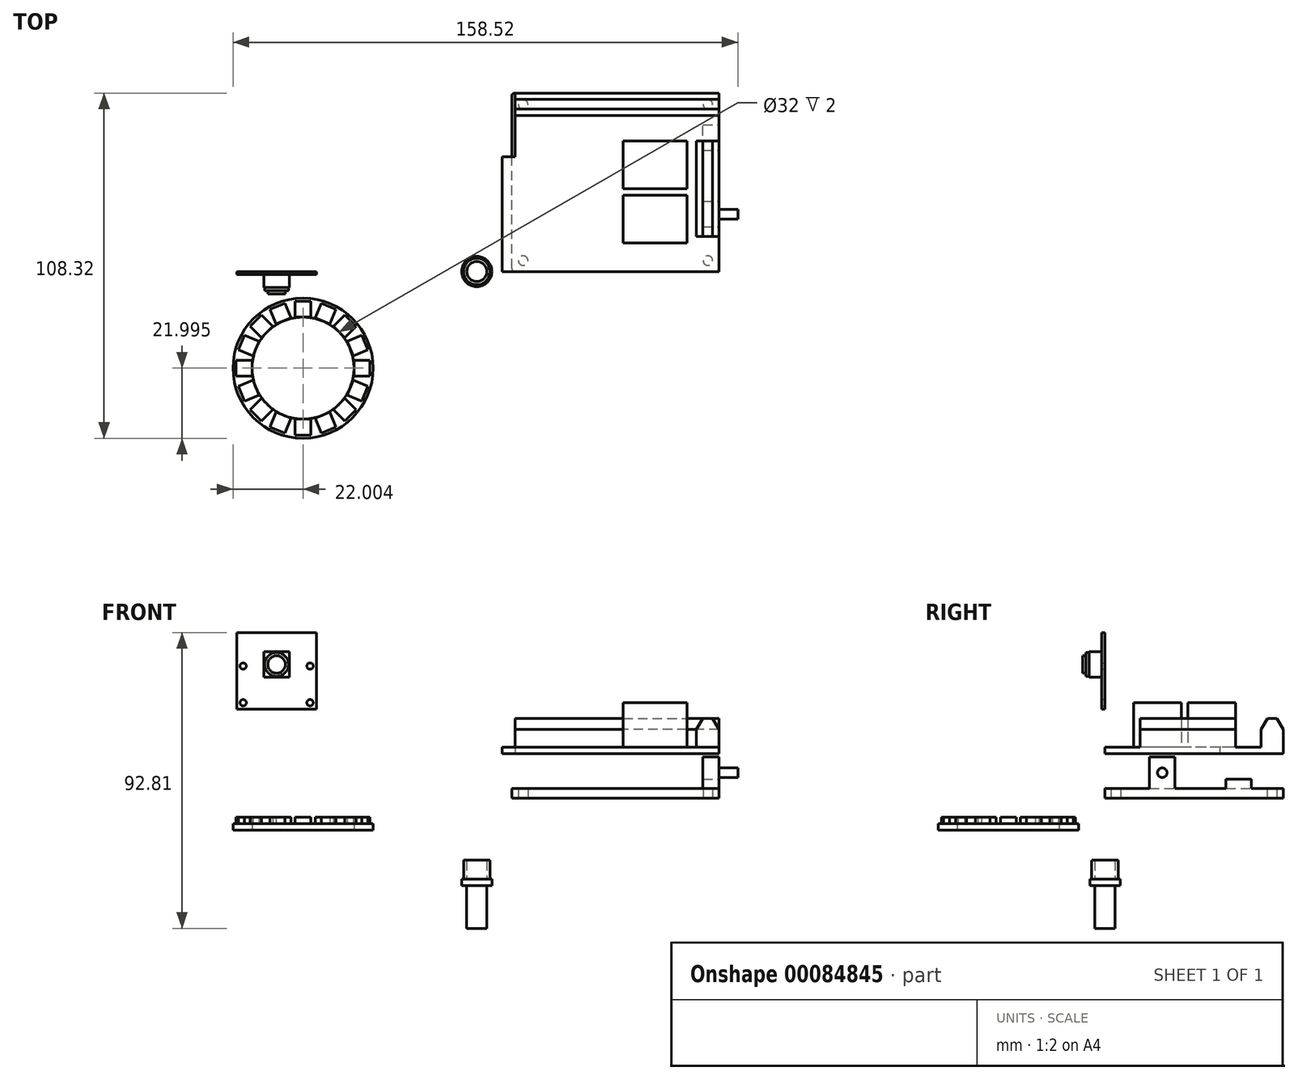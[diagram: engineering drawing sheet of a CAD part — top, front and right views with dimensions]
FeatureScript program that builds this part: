
annotation { "Feature Type Name" : "Feature", "Feature Type Description" : "" }
export const myFeature = defineFeature(function(context is Context, id is Id, definition is map)
    precondition{}
    {
        {
            var Q0;
            Q0=qCreatedBy(makeId("Top.planeOp"),FACE);
            cPlane(context, id + "F0", {"entities" : qUnion([Q0]), "cplaneType" : CPlaneType.OFFSET, "offset" : 10 * mm, "width" : 150 * mm, "height" : 150 * mm});
        }
        {
            var Q0;
            Q0=qCreatedBy(id+"F0.planeOp",FACE);
            var sketch = newSketch(context, id + "F1", { "sketchPlane" : qUnion([Q0])});
            skLineSegment(sketch, "E0.bottom", {"start": v(21, 0) * mm, "end": v(84, 0) * mm});
            skLineSegment(sketch, "E0.top", {"start": v(21, 56) * mm, "end": v(84, 56) * mm});
            skLineSegment(sketch, "E0.left", {"start": v(20, 1) * mm, "end": v(20, 55) * mm});
            skLineSegment(sketch, "E0.right", {"start": v(85, 1) * mm, "end": v(85, 55) * mm});
            skCircle(sketch, "E1", {"center": v(23.58, 52.42) * mm, "radius": 1.5 * mm});
            skCircle(sketch, "E2.0.1.0", {"center": v(23.58, 3.42) * mm, "radius": 1.5 * mm});
            skCircle(sketch, "E2.1.0.0", {"center": v(81.58, 52.42) * mm, "radius": 1.5 * mm});
            skCircle(sketch, "E2.1.1.0", {"center": v(81.58, 3.42) * mm, "radius": 1.5 * mm});
            skLineSegment(sketch, "E2.direction1", {"start": v(23.58, 52.42) * mm, "end": v(81.58, 52.42) * mm, "construction": true});
            skLineSegment(sketch, "E2.direction2", {"start": v(23.58, 52.42) * mm, "end": v(23.58, 3.42) * mm, "construction": true});
            skPoint(sketch, "E3.visualSharp", {"position": v(85, 56) * mm});
            skArc(sketch, "E3.filletArc", {"start": v(85, 55) * mm, "mid": v(84.7, 55.7) * mm, "end": v(84, 56) * mm});
            skPoint(sketch, "E4.visualSharp", {"position": v(85, 0) * mm});
            skArc(sketch, "E4.filletArc", {"start": v(84, 0) * mm, "mid": v(84.7, 0.3) * mm, "end": v(85, 1) * mm});
            skPoint(sketch, "E5.visualSharp", {"position": v(20, 0) * mm});
            skArc(sketch, "E5.filletArc", {"start": v(20, 1) * mm, "mid": v(20.3, 0.3) * mm, "end": v(21, 0) * mm});
            skPoint(sketch, "E6.visualSharp", {"position": v(20, 56) * mm});
            skArc(sketch, "E6.filletArc", {"start": v(21, 56) * mm, "mid": v(20.3, 55.7) * mm, "end": v(20, 55) * mm});
            skSolve(sketch);
        }
        {
            var Q0;
            Q0=qSketchRegion(id+"F1",true);
            extrude(context, id + "F2", {"entities" : qUnion([Q0]), "depth" : 3 * mm});
        }
        {
            var Q0;
            Q0=makeQuery(id+"F2.opExtrude","SWEPT_FACE",FACE,{"disambiguationData":[OSD([sQuery(id+"F1.wireOp",EDGE,"E0.right")])]});
            var sketch = newSketch(context, id + "F3", { "sketchPlane" : qUnion([Q0])});
            skLineSegment(sketch, "E7.bottom", {"start": v(14, 13) * mm, "end": v(22, 13) * mm});
            skLineSegment(sketch, "E7.top", {"start": v(14, 23) * mm, "end": v(22, 23) * mm});
            skLineSegment(sketch, "E7.left", {"start": v(14, 13) * mm, "end": v(14, 23) * mm});
            skLineSegment(sketch, "E7.right", {"start": v(22, 13) * mm, "end": v(22, 23) * mm});
            skLineSegment(sketch, "E8.bottom", {"start": v(38, 13) * mm, "end": v(46, 13) * mm});
            skLineSegment(sketch, "E8.top", {"start": v(38, 16) * mm, "end": v(46, 16) * mm});
            skLineSegment(sketch, "E8.left", {"start": v(38, 13) * mm, "end": v(38, 16) * mm});
            skLineSegment(sketch, "E8.right", {"start": v(46, 13) * mm, "end": v(46, 16) * mm});
            skSolve(sketch);
        }
        {
            var Q0;
            Q0=qSketchRegion(id+"F3",true);
            extrude(context, id + "F4", {"entities" : qUnion([Q0]), "operationType" : NewBodyOperationType.ADD, "oppositeDirection" : true, "depth" : 5 * mm});
        }
        {
            var Q0;
            Q0=makeQuery(id+"F4.boolean.opBoolean","MERGE",FACE,{"derivedFrom":[makeQuery(id+"F2.opExtrude","SWEPT_FACE",FACE,{"disambiguationData":[OSD([sQuery(id+"F1.wireOp",EDGE,"E0.right")])]}),makeQuery(id+"F4.opExtrude","CAP_FACE",FACE,{"disambiguationData":[OSD([sQuery(id+"F3.wireOp",EDGE,"E7.bottom"),sQuery(id+"F3.wireOp",EDGE,"E7.top"),sQuery(id+"F3.wireOp",EDGE,"E7.left"),sQuery(id+"F3.wireOp",EDGE,"E7.right")])],"isStart":true}),makeQuery(id+"F4.opExtrude","CAP_FACE",FACE,{"disambiguationData":[OSD([sQuery(id+"F3.wireOp",EDGE,"E8.bottom"),sQuery(id+"F3.wireOp",EDGE,"E8.top"),sQuery(id+"F3.wireOp",EDGE,"E8.left"),sQuery(id+"F3.wireOp",EDGE,"E8.right")])],"isStart":true})]});
            var sketch = newSketch(context, id + "F5", { "sketchPlane" : qUnion([Q0])});
            skLineSegment(sketch, "E9", {"start": v(14, 18) * mm, "end": v(18, 18) * mm, "construction": true});
            skLineSegment(sketch, "E10", {"start": v(18, 18) * mm, "end": v(18, 23) * mm, "construction": true});
            skCircle(sketch, "E11", {"center": v(18, 18) * mm, "radius": 1.5 * mm});
            skPoint(sketch, "E12", {"position": v(14, 18) * mm});
            skPoint(sketch, "E13", {"position": v(18, 23) * mm});
            skSolve(sketch);
        }
        {
            var Q0;
            Q0=qSketchRegion(id+"F5",true);
            extrude(context, id + "F6", {"entities" : qUnion([Q0]), "operationType" : NewBodyOperationType.ADD, "depth" : 6 * mm});
        }
        {
            var Q0;
            Q0=qCreatedBy(makeId("Top.planeOp"),FACE);
            var sketch = newSketch(context, id + "F7", { "sketchPlane" : qUnion([Q0])});
            skCircle(sketch, "E14", {"center": v(-45.52, -30.32) * mm, "radius": 22 * mm});
            skCircle(sketch, "E15", {"center": v(-45.52, -30.32) * mm, "radius": 16 * mm});
            skSolve(sketch);
        }
        {
            var Q0;
            Q0=makeQuery(id+"F7.imprint","IMPRINT",FACE,{"disambiguationData":[TD([[makeQuery(id+"F7.imprint","IMPRINT",EDGE,{"derivedFrom":sQuery(id+"F7.wireOp",EDGE,"E14")}),1.0]])]});
            extrude(context, id + "F8", {"entities" : qUnion([Q0]), "depth" : 2 * mm});
        }
        {
            var Q0;
            Q0=makeQuery(id+"F8.opExtrude","CAP_FACE",FACE,{"disambiguationData":[OSD([sQuery(id+"F7.wireOp",EDGE,"E14"),sQuery(id+"F7.wireOp",EDGE,"E15")])],"isStart":false});
            var sketch = newSketch(context, id + "F9", { "sketchPlane" : qUnion([Q0])});
            skLineSegment(sketch, "E16", {"start": v(-69.53, -30.32) * mm, "end": v(-35.4, -30.32) * mm, "construction": true});
            skLineSegment(sketch, "E17", {"start": v(-45.52, -18.96) * mm, "end": v(-45.52, -40.27) * mm, "construction": true});
            skPoint(sketch, "E18", {"position": v(-45.52, -30.32) * mm});
            skLineSegment(sketch, "E19.rect.bottom", {"start": v(-61.52, -27.82) * mm, "end": v(-66.52, -27.82) * mm});
            skLineSegment(sketch, "E19.rect.top", {"start": v(-61.52, -32.82) * mm, "end": v(-66.52, -32.82) * mm});
            skLineSegment(sketch, "E19.rect.left", {"start": v(-61.52, -27.82) * mm, "end": v(-61.52, -32.82) * mm});
            skLineSegment(sketch, "E19.rect.right", {"start": v(-66.52, -27.82) * mm, "end": v(-66.52, -32.82) * mm});
            skPoint(sketch, "E19.rect.middle", {"position": v(-64.02, -30.32) * mm});
            skPoint(sketch, "E20.1.0", {"position": v(-62.6, -37.4) * mm});
            skLineSegment(sketch, "E20.1.1", {"start": v(-61.25, -34.14) * mm, "end": v(-65.87, -36.05) * mm});
            skLineSegment(sketch, "E20.1.2", {"start": v(-61.25, -34.14) * mm, "end": v(-59.34, -38.76) * mm});
            skLineSegment(sketch, "E20.1.3", {"start": v(-59.34, -38.76) * mm, "end": v(-63.96, -40.67) * mm});
            skLineSegment(sketch, "E20.1.4", {"start": v(-65.87, -36.05) * mm, "end": v(-63.96, -40.67) * mm});
            skPoint(sketch, "E20.2.0", {"position": v(-58.6, -43.4) * mm});
            skLineSegment(sketch, "E20.2.1", {"start": v(-58.6, -39.87) * mm, "end": v(-62.13, -43.4) * mm});
            skLineSegment(sketch, "E20.2.2", {"start": v(-58.6, -39.87) * mm, "end": v(-55.06, -43.4) * mm});
            skLineSegment(sketch, "E20.2.3", {"start": v(-55.06, -43.4) * mm, "end": v(-58.6, -46.94) * mm});
            skLineSegment(sketch, "E20.2.4", {"start": v(-62.13, -43.4) * mm, "end": v(-58.6, -46.94) * mm});
            skPoint(sketch, "E20.3.0", {"position": v(-52.6, -47.42) * mm});
            skLineSegment(sketch, "E20.3.1", {"start": v(-53.95, -44.15) * mm, "end": v(-55.86, -48.77) * mm});
            skLineSegment(sketch, "E20.3.2", {"start": v(-53.95, -44.15) * mm, "end": v(-49.33, -46.06) * mm});
            skLineSegment(sketch, "E20.3.3", {"start": v(-49.33, -46.06) * mm, "end": v(-51.24, -50.68) * mm});
            skLineSegment(sketch, "E20.3.4", {"start": v(-55.86, -48.77) * mm, "end": v(-51.24, -50.68) * mm});
            skPoint(sketch, "E20.4.0", {"position": v(-45.52, -48.82) * mm});
            skLineSegment(sketch, "E20.4.1", {"start": v(-48.02, -46.32) * mm, "end": v(-48.02, -51.32) * mm});
            skLineSegment(sketch, "E20.4.2", {"start": v(-48.02, -46.32) * mm, "end": v(-43.02, -46.32) * mm});
            skLineSegment(sketch, "E20.4.3", {"start": v(-43.02, -46.32) * mm, "end": v(-43.02, -51.32) * mm});
            skLineSegment(sketch, "E20.4.4", {"start": v(-48.02, -51.32) * mm, "end": v(-43.02, -51.32) * mm});
            skPoint(sketch, "E20.5.0", {"position": v(-38.44, -47.42) * mm});
            skLineSegment(sketch, "E20.5.1", {"start": v(-41.7, -46.06) * mm, "end": v(-39.79, -50.68) * mm});
            skLineSegment(sketch, "E20.5.2", {"start": v(-41.7, -46.06) * mm, "end": v(-37.08, -44.15) * mm});
            skLineSegment(sketch, "E20.5.3", {"start": v(-37.08, -44.15) * mm, "end": v(-35.17, -48.77) * mm});
            skLineSegment(sketch, "E20.5.4", {"start": v(-39.79, -50.68) * mm, "end": v(-35.17, -48.77) * mm});
            skPoint(sketch, "E20.6.0", {"position": v(-32.43, -43.4) * mm});
            skLineSegment(sketch, "E20.6.1", {"start": v(-35.97, -43.4) * mm, "end": v(-32.43, -46.94) * mm});
            skLineSegment(sketch, "E20.6.2", {"start": v(-35.97, -43.4) * mm, "end": v(-32.43, -39.87) * mm});
            skLineSegment(sketch, "E20.6.3", {"start": v(-32.43, -39.87) * mm, "end": v(-28.9, -43.4) * mm});
            skLineSegment(sketch, "E20.6.4", {"start": v(-32.43, -46.94) * mm, "end": v(-28.9, -43.4) * mm});
            skPoint(sketch, "E20.7.0", {"position": v(-28.42, -37.4) * mm});
            skLineSegment(sketch, "E20.7.1", {"start": v(-31.7, -38.76) * mm, "end": v(-27.07, -40.67) * mm});
            skLineSegment(sketch, "E20.7.2", {"start": v(-31.7, -38.76) * mm, "end": v(-29.78, -34.14) * mm});
            skLineSegment(sketch, "E20.7.3", {"start": v(-29.78, -34.14) * mm, "end": v(-25.16, -36.05) * mm});
            skLineSegment(sketch, "E20.7.4", {"start": v(-27.07, -40.67) * mm, "end": v(-25.16, -36.05) * mm});
            skPoint(sketch, "E20.8.0", {"position": v(-27.02, -30.32) * mm});
            skLineSegment(sketch, "E20.8.1", {"start": v(-29.52, -32.82) * mm, "end": v(-24.52, -32.82) * mm});
            skLineSegment(sketch, "E20.8.2", {"start": v(-29.52, -32.82) * mm, "end": v(-29.52, -27.82) * mm});
            skLineSegment(sketch, "E20.8.3", {"start": v(-29.52, -27.82) * mm, "end": v(-24.52, -27.82) * mm});
            skLineSegment(sketch, "E20.8.4", {"start": v(-24.52, -32.82) * mm, "end": v(-24.52, -27.82) * mm});
            skPoint(sketch, "E20.9.0", {"position": v(-28.42, -23.25) * mm});
            skLineSegment(sketch, "E20.9.1", {"start": v(-29.78, -26.51) * mm, "end": v(-25.16, -24.6) * mm});
            skLineSegment(sketch, "E20.9.2", {"start": v(-29.78, -26.51) * mm, "end": v(-31.7, -21.9) * mm});
            skLineSegment(sketch, "E20.9.3", {"start": v(-31.7, -21.9) * mm, "end": v(-27.07, -19.98) * mm});
            skLineSegment(sketch, "E20.9.4", {"start": v(-25.16, -24.6) * mm, "end": v(-27.07, -19.98) * mm});
            skPoint(sketch, "E20.10.0", {"position": v(-32.43, -17.24) * mm});
            skLineSegment(sketch, "E20.10.1", {"start": v(-32.43, -20.78) * mm, "end": v(-28.9, -17.24) * mm});
            skLineSegment(sketch, "E20.10.2", {"start": v(-32.43, -20.78) * mm, "end": v(-35.97, -17.24) * mm});
            skLineSegment(sketch, "E20.10.3", {"start": v(-35.97, -17.24) * mm, "end": v(-32.43, -13.7) * mm});
            skLineSegment(sketch, "E20.10.4", {"start": v(-28.9, -17.24) * mm, "end": v(-32.43, -13.7) * mm});
            skPoint(sketch, "E20.11.0", {"position": v(-38.44, -13.23) * mm});
            skLineSegment(sketch, "E20.11.1", {"start": v(-37.08, -16.5) * mm, "end": v(-35.17, -11.88) * mm});
            skLineSegment(sketch, "E20.11.2", {"start": v(-37.08, -16.5) * mm, "end": v(-41.7, -14.59) * mm});
            skLineSegment(sketch, "E20.11.3", {"start": v(-41.7, -14.59) * mm, "end": v(-39.79, -9.97) * mm});
            skLineSegment(sketch, "E20.11.4", {"start": v(-35.17, -11.88) * mm, "end": v(-39.79, -9.97) * mm});
            skPoint(sketch, "E20.12.0", {"position": v(-45.52, -11.82) * mm});
            skLineSegment(sketch, "E20.12.1", {"start": v(-43.02, -14.32) * mm, "end": v(-43.02, -9.32) * mm});
            skLineSegment(sketch, "E20.12.2", {"start": v(-43.02, -14.32) * mm, "end": v(-48.02, -14.32) * mm});
            skLineSegment(sketch, "E20.12.3", {"start": v(-48.02, -14.32) * mm, "end": v(-48.02, -9.32) * mm});
            skLineSegment(sketch, "E20.12.4", {"start": v(-43.02, -9.32) * mm, "end": v(-48.02, -9.32) * mm});
            skPoint(sketch, "E20.13.0", {"position": v(-52.6, -13.23) * mm});
            skLineSegment(sketch, "E20.13.1", {"start": v(-49.33, -14.59) * mm, "end": v(-51.24, -9.97) * mm});
            skLineSegment(sketch, "E20.13.2", {"start": v(-49.33, -14.59) * mm, "end": v(-53.95, -16.5) * mm});
            skLineSegment(sketch, "E20.13.3", {"start": v(-53.95, -16.5) * mm, "end": v(-55.86, -11.88) * mm});
            skLineSegment(sketch, "E20.13.4", {"start": v(-51.24, -9.97) * mm, "end": v(-55.86, -11.88) * mm});
            skPoint(sketch, "E20.14.0", {"position": v(-58.6, -17.24) * mm});
            skLineSegment(sketch, "E20.14.1", {"start": v(-55.06, -17.24) * mm, "end": v(-58.6, -13.7) * mm});
            skLineSegment(sketch, "E20.14.2", {"start": v(-55.06, -17.24) * mm, "end": v(-58.6, -20.78) * mm});
            skLineSegment(sketch, "E20.14.3", {"start": v(-58.6, -20.78) * mm, "end": v(-62.13, -17.24) * mm});
            skLineSegment(sketch, "E20.14.4", {"start": v(-58.6, -13.7) * mm, "end": v(-62.13, -17.24) * mm});
            skPoint(sketch, "E20.15.0", {"position": v(-62.6, -23.25) * mm});
            skLineSegment(sketch, "E20.15.1", {"start": v(-59.34, -21.9) * mm, "end": v(-63.96, -19.98) * mm});
            skLineSegment(sketch, "E20.15.2", {"start": v(-59.34, -21.9) * mm, "end": v(-61.25, -26.51) * mm});
            skLineSegment(sketch, "E20.15.3", {"start": v(-61.25, -26.51) * mm, "end": v(-65.87, -24.6) * mm});
            skLineSegment(sketch, "E20.15.4", {"start": v(-63.96, -19.98) * mm, "end": v(-65.87, -24.6) * mm});
            skSolve(sketch);
        }
        {
            var Q0;
            Q0=qSketchRegion(id+"F9",true);
            extrude(context, id + "F10", {"entities" : qUnion([Q0]), "operationType" : NewBodyOperationType.ADD, "depth" : 2 * mm});
        }
        {
            var Q0;
            Q0=makeQuery(id+"F2.opExtrude","CAP_FACE",FACE,{"disambiguationData":[OSD([sQuery(id+"F1.wireOp",EDGE,"E0.bottom"),sQuery(id+"F1.wireOp",EDGE,"E0.top"),sQuery(id+"F1.wireOp",EDGE,"E0.left"),sQuery(id+"F1.wireOp",EDGE,"E0.right"),sQuery(id+"F1.wireOp",EDGE,"E1"),sQuery(id+"F1.wireOp",EDGE,"E2.0.1.0"),sQuery(id+"F1.wireOp",EDGE,"E2.1.0.0"),sQuery(id+"F1.wireOp",EDGE,"E2.1.1.0"),sQuery(id+"F1.wireOp",EDGE,"E3.filletArc"),sQuery(id+"F1.wireOp",EDGE,"E4.filletArc"),sQuery(id+"F1.wireOp",EDGE,"E5.filletArc"),sQuery(id+"F1.wireOp",EDGE,"E6.filletArc")])],"isStart":false});
            cPlane(context, id + "F11", {"entities" : qUnion([Q0]), "cplaneType" : CPlaneType.OFFSET, "offset" : 11 * mm, "width" : 150 * mm, "height" : 150 * mm});
        }
        {
            var Q0;
            Q0=qCreatedBy(id+"F11.planeOp",FACE);
            var sketch = newSketch(context, id + "F12", { "sketchPlane" : qUnion([Q0])});
            skLineSegment(sketch, "E21", {"start": v(85, 56) * mm, "end": v(21, 56) * mm});
            skLineSegment(sketch, "E22", {"start": v(21, 56) * mm, "end": v(21, 36) * mm});
            skLineSegment(sketch, "E23", {"start": v(21, 36) * mm, "end": v(17, 36) * mm});
            skLineSegment(sketch, "E24", {"start": v(17, 36) * mm, "end": v(17, 0) * mm});
            skLineSegment(sketch, "E25", {"start": v(17, 0) * mm, "end": v(85, 0) * mm});
            skLineSegment(sketch, "E26", {"start": v(85, 0) * mm, "end": v(85, 56) * mm});
            skSolve(sketch);
        }
        {
            var Q0;
            Q0=qSketchRegion(id+"F12",true);
            extrude(context, id + "F13", {"entities" : qUnion([Q0]), "depth" : 2 * mm});
        }
        {
            var Q0;
            Q0=makeQuery(id+"F13.opExtrude","CAP_FACE",FACE,{"disambiguationData":[OSD([sQuery(id+"F12.wireOp",EDGE,"E21"),sQuery(id+"F12.wireOp",EDGE,"E22"),sQuery(id+"F12.wireOp",EDGE,"E23"),sQuery(id+"F12.wireOp",EDGE,"E24"),sQuery(id+"F12.wireOp",EDGE,"E25"),sQuery(id+"F12.wireOp",EDGE,"E26")])],"isStart":false});
            var sketch = newSketch(context, id + "F14", { "sketchPlane" : qUnion([Q0])});
            skLineSegment(sketch, "E27.bottom", {"start": v(21, 56) * mm, "end": v(85, 56) * mm});
            skLineSegment(sketch, "E27.top", {"start": v(21, 49) * mm, "end": v(85, 49) * mm});
            skLineSegment(sketch, "E27.left", {"start": v(21, 56) * mm, "end": v(21, 49) * mm});
            skLineSegment(sketch, "E27.right", {"start": v(85, 56) * mm, "end": v(85, 49) * mm});
            skLineSegment(sketch, "E28.bottom", {"start": v(85, 41) * mm, "end": v(78, 41) * mm});
            skLineSegment(sketch, "E28.top", {"start": v(85, 11) * mm, "end": v(78, 11) * mm});
            skLineSegment(sketch, "E28.left", {"start": v(85, 41) * mm, "end": v(85, 11) * mm});
            skLineSegment(sketch, "E28.right", {"start": v(78, 41) * mm, "end": v(78, 11) * mm});
            skSolve(sketch);
        }
        {
            var Q0;
            Q0=qSketchRegion(id+"F14",true);
            extrude(context, id + "F15", {"entities" : qUnion([Q0]), "operationType" : NewBodyOperationType.ADD, "depth" : 9 * mm});
        }
        {
            var Q0;
            Q0=makeQuery(id+"F15.opExtrude","CAP_EDGE",EDGE,{"disambiguationData":[OSD([sQuery(id+"F14.wireOp",EDGE,"E28.right")])],"isStart":false});
            var Q1;
            Q1=makeQuery(id+"F15.opExtrude","CAP_EDGE",EDGE,{"disambiguationData":[OSD([sQuery(id+"F14.wireOp",EDGE,"E27.top")])],"isStart":false});
            var Q2;
            Q2=makeQuery(id+"F15.opExtrude","CAP_EDGE",EDGE,{"disambiguationData":[OSD([sQuery(id+"F14.wireOp",EDGE,"E28.left")])],"isStart":false});
            var Q3;
            Q3=makeQuery(id+"F15.opExtrude","CAP_EDGE",EDGE,{"disambiguationData":[OSD([sQuery(id+"F14.wireOp",EDGE,"E27.bottom")])],"isStart":false});
            chamfer(context, id + "F16", {"entities" : qUnion([Q0, Q1, Q2, Q3]), "chamferType" : ChamferType.OFFSET_ANGLE, "width" : 2 * mm, "oppositeDirection" : false, "angle" : 60 * degree, "tangentPropagation" : true});
        }
        {
            var Q0;
            Q0=qCreatedBy(id+"F11.planeOp",FACE);
            var sketch = newSketch(context, id + "F17", { "sketchPlane" : qUnion([Q0])});
            skLineSegment(sketch, "E29.bottom", {"start": v(55, 26) * mm, "end": v(75, 26) * mm});
            skLineSegment(sketch, "E29.top", {"start": v(55, 41) * mm, "end": v(75, 41) * mm});
            skLineSegment(sketch, "E29.left", {"start": v(55, 26) * mm, "end": v(55, 41) * mm});
            skLineSegment(sketch, "E29.right", {"start": v(75, 26) * mm, "end": v(75, 41) * mm});
            skLineSegment(sketch, "E30.bottom", {"start": v(55, 9) * mm, "end": v(75, 9) * mm});
            skLineSegment(sketch, "E30.top", {"start": v(55, 24) * mm, "end": v(75, 24) * mm});
            skLineSegment(sketch, "E30.left", {"start": v(55, 9) * mm, "end": v(55, 24) * mm});
            skLineSegment(sketch, "E30.right", {"start": v(75, 9) * mm, "end": v(75, 24) * mm});
            skSolve(sketch);
        }
        {
            var Q0;
            Q0=qSketchRegion(id+"F17",true);
            extrude(context, id + "F18", {"entities" : qUnion([Q0]), "operationType" : NewBodyOperationType.ADD, "depth" : 16 * mm});
        }
        {
            var Q0;
            Q0=qCreatedBy(makeId("Front.planeOp"),FACE);
            var sketch = newSketch(context, id + "F19", { "sketchPlane" : qUnion([Q0])});
            skLineSegment(sketch, "E31", {"start": v(12.47, -9.4) * mm, "end": v(12.87, -9.4) * mm});
            skLineSegment(sketch, "E32", {"start": v(13.17, -9.7) * mm, "end": v(13.17, -15.4) * mm});
            skLineSegment(sketch, "E33", {"start": v(13.17, -15.4) * mm, "end": v(13.77, -15.4) * mm});
            skLineSegment(sketch, "E34", {"start": v(13.77, -15.4) * mm, "end": v(13.77, -17.4) * mm});
            skLineSegment(sketch, "E35", {"start": v(13.77, -17.4) * mm, "end": v(12.17, -17.4) * mm});
            skLineSegment(sketch, "E36", {"start": v(12.17, -17.4) * mm, "end": v(12.17, -30.84) * mm});
            skLineSegment(sketch, "E37", {"start": v(12.17, -30.84) * mm, "end": v(9.02, -30.84) * mm});
            skLineSegment(sketch, "E38", {"start": v(9.02, -30.84) * mm, "end": v(9.02, -15.4) * mm});
            skLineSegment(sketch, "E39", {"start": v(9.02, -15.4) * mm, "end": v(12.17, -15.4) * mm});
            skLineSegment(sketch, "E40", {"start": v(12.17, -15.4) * mm, "end": v(12.17, -9.7) * mm});
            skLineSegment(sketch, "E41", {"start": v(12.17, -15.4) * mm, "end": v(13.17, -15.4) * mm, "construction": true});
            skPoint(sketch, "E42.visualSharp", {"position": v(13.17, -9.4) * mm});
            skArc(sketch, "E42.filletArc", {"start": v(13.17, -9.7) * mm, "mid": v(13.08, -9.49) * mm, "end": v(12.87, -9.4) * mm});
            skPoint(sketch, "E43.visualSharp", {"position": v(12.17, -9.4) * mm});
            skArc(sketch, "E43.filletArc", {"start": v(12.47, -9.4) * mm, "mid": v(12.26, -9.49) * mm, "end": v(12.17, -9.7) * mm});
            skSolve(sketch);
        }
        {
            var Q0;
            Q0=qSketchRegion(id+"F19",true);
            var Q1;
            Q1=sQuery(id+"F19.wireOp",EDGE,"E38");
            revolve(context, id + "F20", {"entities" : qUnion([Q0]), "axis" : qUnion([Q1]), "revolveType" : RevolveType.FULL});
        }
        {
            var Q0;
            Q0=qCreatedBy(makeId("Front.planeOp"),FACE);
            var sketch = newSketch(context, id + "F21", { "sketchPlane" : qUnion([Q0])});
            skLineSegment(sketch, "E44.bottom", {"start": v(-41.33, 61.97) * mm, "end": v(-66.33, 61.97) * mm});
            skLineSegment(sketch, "E44.top", {"start": v(-41.33, 37.97) * mm, "end": v(-66.33, 37.97) * mm});
            skLineSegment(sketch, "E44.left", {"start": v(-41.33, 61.97) * mm, "end": v(-41.33, 37.97) * mm});
            skLineSegment(sketch, "E44.right", {"start": v(-66.33, 61.97) * mm, "end": v(-66.33, 37.97) * mm});
            skPoint(sketch, "E44.middle", {"position": v(-53.83, 49.97) * mm});
            skCircle(sketch, "E45", {"center": v(-64.33, 39.97) * mm, "radius": 1 * mm});
            skCircle(sketch, "E46.0.1.0", {"center": v(-64.33, 51.47) * mm, "radius": 1 * mm});
            skCircle(sketch, "E46.1.0.0", {"center": v(-43.33, 39.97) * mm, "radius": 1 * mm});
            skCircle(sketch, "E46.1.1.0", {"center": v(-43.33, 51.47) * mm, "radius": 1 * mm});
            skLineSegment(sketch, "E46.direction1", {"start": v(-64.33, 39.97) * mm, "end": v(-43.33, 39.97) * mm, "construction": true});
            skLineSegment(sketch, "E46.direction2", {"start": v(-64.33, 39.97) * mm, "end": v(-64.33, 51.47) * mm, "construction": true});
            skSolve(sketch);
        }
        {
            var Q0;
            Q0=qSketchRegion(id+"F21",true);
            extrude(context, id + "F22", {"entities" : qUnion([Q0]), "depth" : 1 * mm});
        }
        {
            var Q0;
            Q0=makeQuery(id+"F22.opExtrude","CAP_FACE",FACE,{"disambiguationData":[OSD([sQuery(id+"F21.wireOp",EDGE,"E44.bottom"),sQuery(id+"F21.wireOp",EDGE,"E44.top"),sQuery(id+"F21.wireOp",EDGE,"E44.left"),sQuery(id+"F21.wireOp",EDGE,"E44.right"),sQuery(id+"F21.wireOp",EDGE,"E45"),sQuery(id+"F21.wireOp",EDGE,"E46.0.1.0"),sQuery(id+"F21.wireOp",EDGE,"E46.1.0.0"),sQuery(id+"F21.wireOp",EDGE,"E46.1.1.0")])],"isStart":false});
            var sketch = newSketch(context, id + "F23", { "sketchPlane" : qUnion([Q0])});
            skLineSegment(sketch, "E47", {"start": v(-53.83, 61.97) * mm, "end": v(-53.83, 37.97) * mm, "construction": true});
            skLineSegment(sketch, "E48.bottom", {"start": v(-49.83, 55.97) * mm, "end": v(-57.83, 55.97) * mm});
            skLineSegment(sketch, "E48.top", {"start": v(-49.83, 47.97) * mm, "end": v(-57.83, 47.97) * mm});
            skLineSegment(sketch, "E48.left", {"start": v(-49.83, 55.97) * mm, "end": v(-49.83, 47.97) * mm});
            skLineSegment(sketch, "E48.right", {"start": v(-57.83, 55.97) * mm, "end": v(-57.83, 47.97) * mm});
            skPoint(sketch, "E48.middle", {"position": v(-53.83, 51.97) * mm});
            skSolve(sketch);
        }
        {
            var Q0;
            Q0=qSketchRegion(id+"F23",true);
            extrude(context, id + "F24", {"entities" : qUnion([Q0]), "operationType" : NewBodyOperationType.ADD, "depth" : 4 * mm});
        }
        {
            var Q0;
            Q0=makeQuery(id+"F24.opExtrude","CAP_FACE",FACE,{"disambiguationData":[OSD([sQuery(id+"F23.wireOp",EDGE,"E48.bottom"),sQuery(id+"F23.wireOp",EDGE,"E48.top"),sQuery(id+"F23.wireOp",EDGE,"E48.left"),sQuery(id+"F23.wireOp",EDGE,"E48.right")])],"isStart":false});
            var sketch = newSketch(context, id + "F25", { "sketchPlane" : qUnion([Q0])});
            skLineSegment(sketch, "E49", {"start": v(-57.83, 51.97) * mm, "end": v(-49.83, 51.97) * mm, "construction": true});
            skCircle(sketch, "E50", {"center": v(-53.83, 51.97) * mm, "radius": 3.75 * mm});
            skSolve(sketch);
        }
        {
            var Q0;
            Q0=qSketchRegion(id+"F25",true);
            extrude(context, id + "F26", {"entities" : qUnion([Q0]), "operationType" : NewBodyOperationType.ADD, "depth" : 1 * mm});
        }
        {
            var Q0;
            Q0=makeQuery(id+"F26.opExtrude","CAP_FACE",FACE,{"disambiguationData":[OSD([sQuery(id+"F25.wireOp",EDGE,"E50")])],"isStart":false});
            var sketch = newSketch(context, id + "F27", { "sketchPlane" : qUnion([Q0])});
            skCircle(sketch, "E51", {"center": v(-53.83, 51.97) * mm, "radius": 2.75 * mm});
            skSolve(sketch);
        }
        {
            var Q0;
            Q0=qSketchRegion(id+"F27",true);
            extrude(context, id + "F28", {"entities" : qUnion([Q0]), "operationType" : NewBodyOperationType.ADD, "depth" : 1 * mm});
        }
    });
